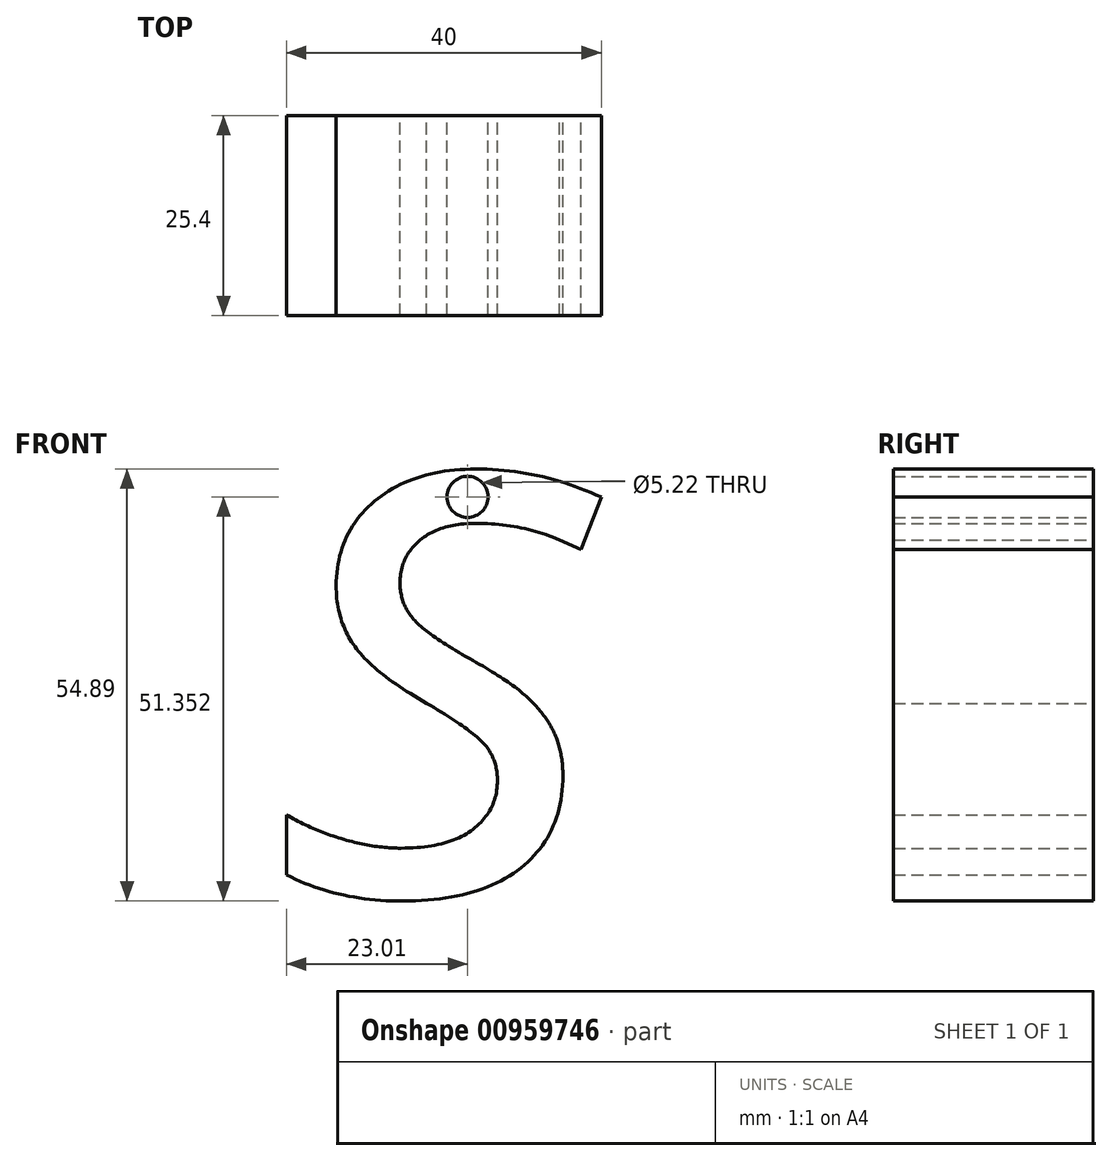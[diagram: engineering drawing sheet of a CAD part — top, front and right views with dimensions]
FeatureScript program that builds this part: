
annotation { "Feature Type Name" : "Feature", "Feature Type Description" : "" }
export const myFeature = defineFeature(function(context is Context, id is Id, definition is map)
    precondition{}
    {
        {
            var Q0;
            Q0=qCreatedBy(makeId("Front.planeOp"),FACE);
            var sketch = newSketch(context, id + "F0", { "sketchPlane" : qUnion([Q0])});
            skText(sketch, "E0", { "text": "s", "fontName": "OpenSans-Italic.ttf"});
            skCircle(sketch, "E1", {"center": v(0, 50.38) * mm, "radius": 2.6 * mm});
            const initialGuessF0  = {"E0": [-0.0234, 0, 1, 0, 0.07123]};
            skSetInitialGuess(sketch, initialGuessF0);
            skSolve(sketch);
        }
        {
            var Q0;
            Q0 = qSketchRegion(id + "F0", true);
            extrude(context, id + "F1", {"entities" : qUnion([Q0]), "depth" : 25.4 * mm, "offsetDistance" : 25.4 * mm});
        }
    });
